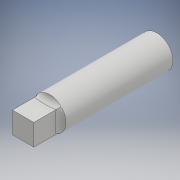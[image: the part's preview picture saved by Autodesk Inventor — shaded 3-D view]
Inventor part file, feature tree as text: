
AUTODESK INVENTOR PART (.ipt)
format: ipt  version: 2018 (Build 220112000, 112)  size: 190,976 bytes
history: native  units: mm
features: extrude x2, sketch x2, fillet x1
ambient origin geometry x8: Origin, YZ Plane, XZ Plane, XY Plane, X Axis, Y Axis, Z Axis, Center Point
bodies: Solid1 (feature_tree)
feature tree (5):
  extrude  "Extrusion1"  Depth=8.0mm
  extrude  "Extrusion2"  Depth=12.0mm
  fillet  "Fillet1"  Radius=40.0mm
  sketch  "Sketch1"  dims[d0=8.0mm d1=8.0mm]
  sketch  "Sketch2"  dims[d2=10.0mm d3=0.0mm d4=12.0mm d5=40.0mm d6=0.0mm d7=2.0mm]
